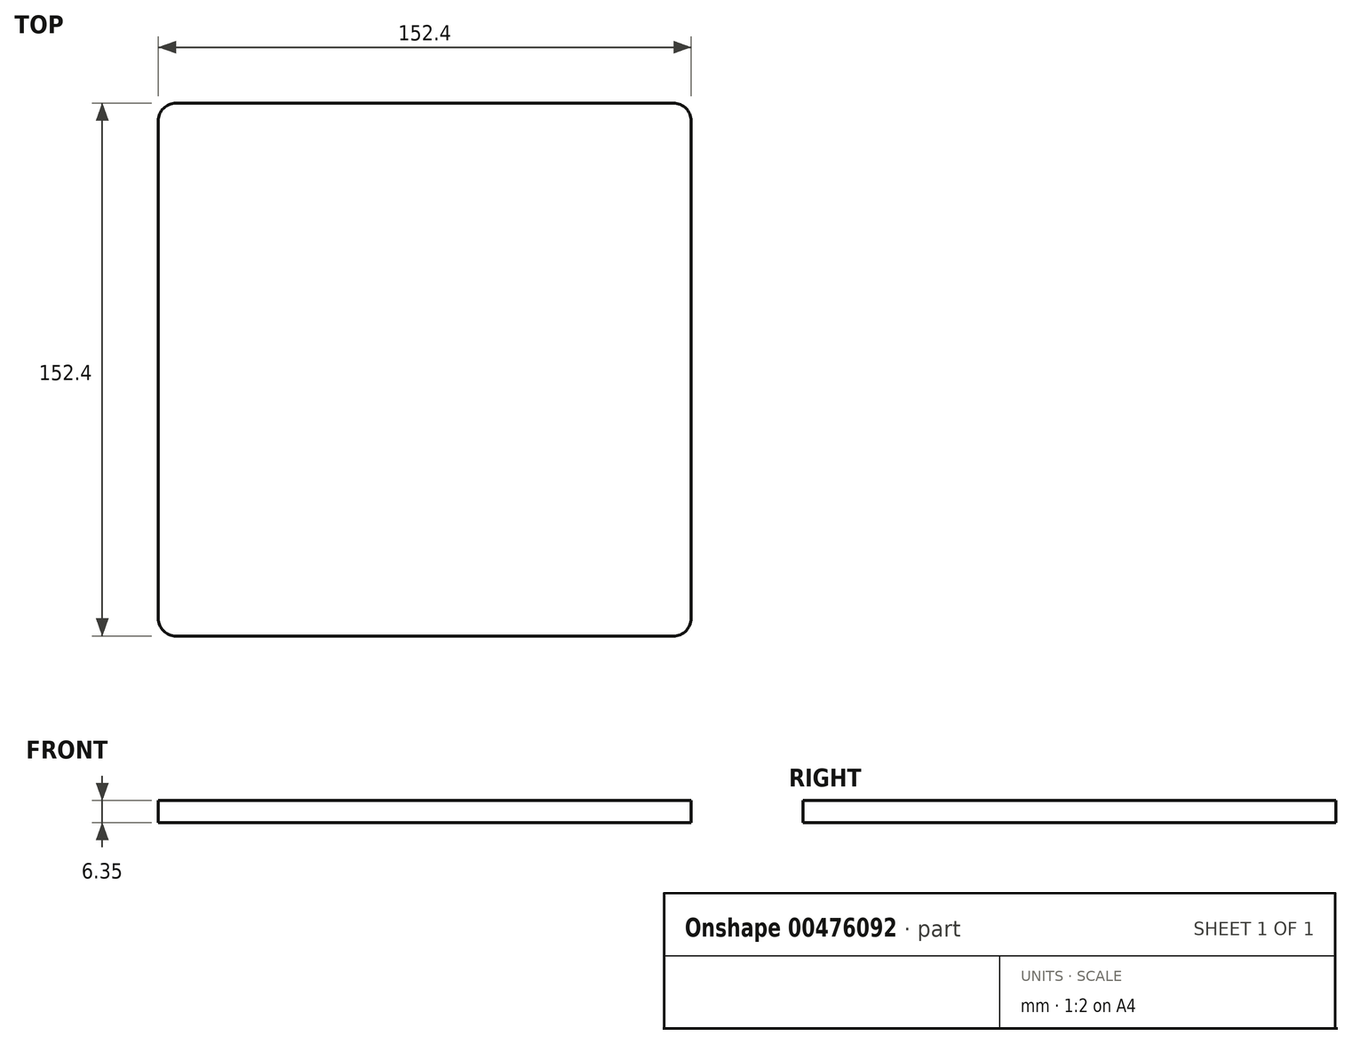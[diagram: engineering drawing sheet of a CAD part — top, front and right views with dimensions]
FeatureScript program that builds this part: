
annotation { "Feature Type Name" : "Feature", "Feature Type Description" : "" }
export const myFeature = defineFeature(function(context is Context, id is Id, definition is map)
    precondition{}
    {
        {
            var Q0;
            Q0=qCreatedBy(makeId("Top.planeOp"),FACE);
            var sketch = newSketch(context, id + "F0", { "sketchPlane" : qUnion([Q0])});
            skLineSegment(sketch, "E0.bottom", {"start": v(-76.2, 76.2) * mm, "end": v(76.2, 76.2) * mm});
            skLineSegment(sketch, "E0.top", {"start": v(-76.2, -76.2) * mm, "end": v(76.2, -76.2) * mm});
            skLineSegment(sketch, "E0.left", {"start": v(-76.2, 76.2) * mm, "end": v(-76.2, -76.2) * mm});
            skLineSegment(sketch, "E0.right", {"start": v(76.2, 76.2) * mm, "end": v(76.2, -76.2) * mm});
            skPoint(sketch, "E0.middle", {"position": v(0, 0) * mm});
            skSolve(sketch);
        }
        {
            var Q0;
            Q0 = qSketchRegion(id + "F0", true);
            extrude(context, id + "F1", {"entities" : qUnion([Q0]), "depth" : 6.35 * mm, "offsetDistance" : 25.4 * mm});
        }
        {
            var Q0;
            Q0=makeQuery(id+"F1.opExtrude","SWEPT_EDGE",EDGE,{"disambiguationData":[OSD([sQuery(id+"F0.wireOp",EDGE,"E0.top"),sQuery(id+"F0.wireOp",EDGE,"E0.right")])]});
            var Q1;
            Q1=makeQuery(id+"F1.opExtrude","SWEPT_EDGE",EDGE,{"disambiguationData":[OSD([sQuery(id+"F0.wireOp",EDGE,"E0.top"),sQuery(id+"F0.wireOp",EDGE,"E0.left")])]});
            var Q2;
            Q2=makeQuery(id+"F1.opExtrude","SWEPT_EDGE",EDGE,{"disambiguationData":[OSD([sQuery(id+"F0.wireOp",EDGE,"E0.bottom"),sQuery(id+"F0.wireOp",EDGE,"E0.left")])]});
            var Q3;
            Q3=makeQuery(id+"F1.opExtrude","SWEPT_EDGE",EDGE,{"disambiguationData":[OSD([sQuery(id+"F0.wireOp",EDGE,"E0.bottom"),sQuery(id+"F0.wireOp",EDGE,"E0.right")])]});
            fillet(context, id + "F2", {"entities" : qUnion([Q0, Q1, Q2, Q3]), "radius" : 5.08 * mm, "tangentPropagation" : true, "allowEdgeOverflow" : false});
        }
    });
